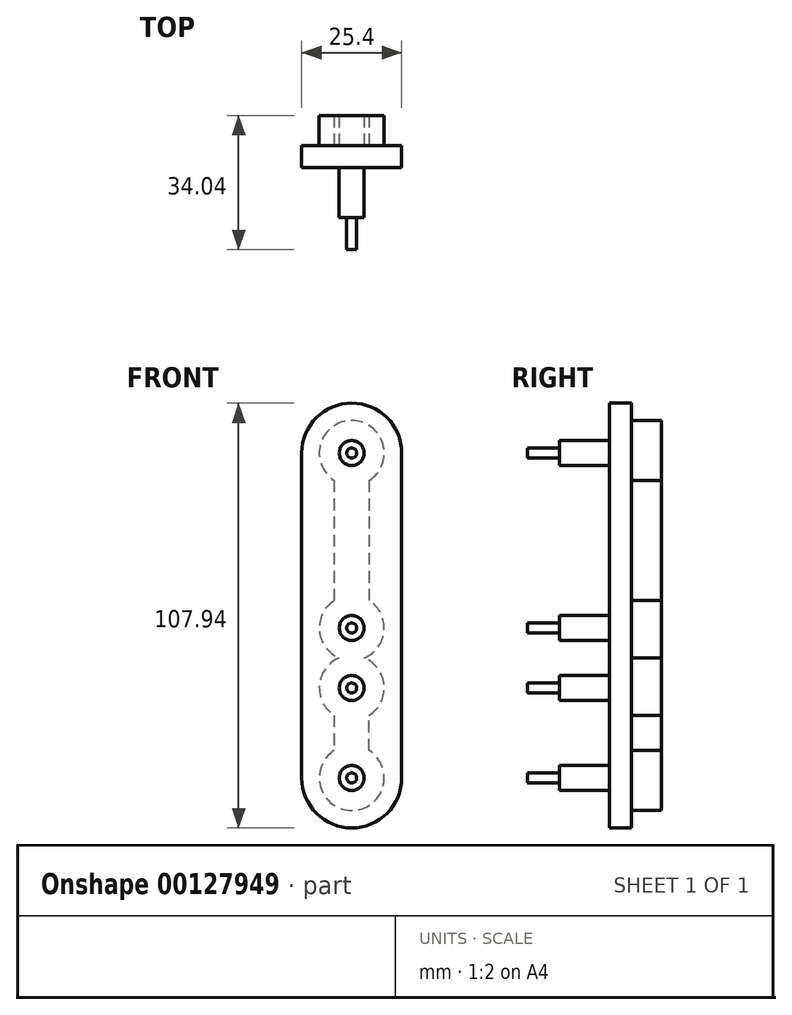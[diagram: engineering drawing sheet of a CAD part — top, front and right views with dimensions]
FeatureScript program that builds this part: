
annotation { "Feature Type Name" : "Feature", "Feature Type Description" : "" }
export const myFeature = defineFeature(function(context is Context, id is Id, definition is map)
    precondition{}
    {
        {
            var Q0;
            Q0=qCreatedBy(makeId("Front.planeOp"),FACE);
            var sketch = newSketch(context, id + "F0", { "sketchPlane" : qUnion([Q0])});
            skArc(sketch, "E0", {"start": v(12.7, 41.28) * mm, "mid": v(0, 53.98) * mm, "end": v(-12.7, 41.28) * mm});
            skArc(sketch, "E1", {"start": v(-12.7, -41.28) * mm, "mid": v(0, -53.98) * mm, "end": v(12.7, -41.28) * mm});
            skLineSegment(sketch, "E2", {"start": v(0, 41.28) * mm, "end": v(0, -41.28) * mm, "construction": true});
            skLineSegment(sketch, "E3", {"start": v(-12.7, 41.28) * mm, "end": v(-12.7, -41.28) * mm});
            skLineSegment(sketch, "E4", {"start": v(12.7, -41.28) * mm, "end": v(12.7, 41.28) * mm});
            skSolve(sketch);
        }
        {
            var Q0;
            Q0 = qSketchRegion(id + "F0", true);
            extrude(context, id + "F1", {"entities" : qUnion([Q0]), "depth" : 5.6 * mm});
        }
        {
            var Q0;
            Q0=makeQuery(id+"F1.opExtrude","CAP_FACE",FACE,{"disambiguationData":[OSD([sQuery(id+"F0.wireOp",EDGE,"E0"),sQuery(id+"F0.wireOp",EDGE,"E1"),sQuery(id+"F0.wireOp",EDGE,"E3"),sQuery(id+"F0.wireOp",EDGE,"E4")])],"isStart":true});
            var sketch = newSketch(context, id + "F2", { "sketchPlane" : qUnion([Q0])});
            skCircle(sketch, "E5", {"center": v(0, 41.28) * mm, "radius": 8.26 * mm});
            skCircle(sketch, "E6", {"center": v(0, -41.28) * mm, "radius": 8.26 * mm});
            skCircle(sketch, "E7", {"center": v(0, -18.42) * mm, "radius": 8.26 * mm});
            skCircle(sketch, "E8", {"center": v(0, -3.18) * mm, "radius": 8.26 * mm});
            skLineSegment(sketch, "E9", {"start": v(-4.44, 34.32) * mm, "end": v(-4.44, 3.78) * mm});
            skLineSegment(sketch, "E10", {"start": v(4.45, 34.32) * mm, "end": v(4.45, 3.78) * mm});
            skLineSegment(sketch, "E11", {"start": v(4.45, -25.37) * mm, "end": v(4.45, -34.32) * mm});
            skLineSegment(sketch, "E12", {"start": v(-4.44, -34.32) * mm, "end": v(-4.44, -25.37) * mm});
            skLineSegment(sketch, "E13", {"start": v(-4.44, 34.32) * mm, "end": v(4.44, 34.32) * mm, "construction": true});
            skSolve(sketch);
        }
        {
            var Q0;
            Q0 = qSketchRegion(id + "F2", true);
            extrude(context, id + "F3", {"entities" : qUnion([Q0]), "operationType" : NewBodyOperationType.ADD, "depth" : 7.62 * mm});
        }
        {
            var Q0;
            Q0=makeQuery(id+"F1.opExtrude","CAP_FACE",FACE,{"disambiguationData":[OSD([sQuery(id+"F0.wireOp",EDGE,"E0"),sQuery(id+"F0.wireOp",EDGE,"E1"),sQuery(id+"F0.wireOp",EDGE,"E3"),sQuery(id+"F0.wireOp",EDGE,"E4")])],"isStart":false});
            var sketch = newSketch(context, id + "F4", { "sketchPlane" : qUnion([Q0])});
            skCircle(sketch, "E14", {"center": v(0, -41.28) * mm, "radius": 3.18 * mm});
            skCircle(sketch, "E15", {"center": v(0, 41.28) * mm, "radius": 3.18 * mm});
            skArc(sketch, "E16.0", {"start": v(-3.17, -10.8) * mm, "mid": v(-8.22, -3.9) * mm, "end": v(-4.45, 3.78) * mm, "construction": true});
            skArc(sketch, "E17.0", {"start": v(-4.45, -25.37) * mm, "mid": v(-8.22, -17.7) * mm, "end": v(-3.18, -10.8) * mm, "construction": true});
            skCircle(sketch, "E18", {"center": v(0, -3.18) * mm, "radius": 3.18 * mm});
            skCircle(sketch, "E19", {"center": v(0, -18.42) * mm, "radius": 3.18 * mm});
            skSolve(sketch);
        }
        {
            var Q0;
            Q0 = qSketchRegion(id + "F4", true);
            extrude(context, id + "F5", {"entities" : qUnion([Q0]), "operationType" : NewBodyOperationType.ADD, "depth" : 12.7 * mm});
        }
        {
            var Q0;
            Q0=makeQuery(id+"F5.opExtrude","CAP_FACE",FACE,{"disambiguationData":[OSD([sQuery(id+"F4.wireOp",EDGE,"E15")])],"isStart":false});
            var sketch = newSketch(context, id + "F6", { "sketchPlane" : qUnion([Q0])});
            skCircle(sketch, "E20", {"center": v(0, 41.28) * mm, "radius": 1.27 * mm});
            skCircle(sketch, "E21.0", {"center": v(0, -3.18) * mm, "radius": 3.18 * mm, "construction": true});
            skCircle(sketch, "E22.0", {"center": v(0, -18.42) * mm, "radius": 3.18 * mm, "construction": true});
            skCircle(sketch, "E23.0", {"center": v(0, -41.28) * mm, "radius": 3.18 * mm, "construction": true});
            skCircle(sketch, "E24", {"center": v(0, -3.18) * mm, "radius": 1.27 * mm});
            skCircle(sketch, "E25", {"center": v(0, -18.42) * mm, "radius": 1.27 * mm});
            skCircle(sketch, "E26", {"center": v(0, -41.28) * mm, "radius": 1.27 * mm});
            skSolve(sketch);
        }
        {
            var Q0;
            Q0 = qSketchRegion(id + "F6", true);
            extrude(context, id + "F7", {"entities" : qUnion([Q0]), "operationType" : NewBodyOperationType.ADD, "depth" : 8.13 * mm});
        }
    });
